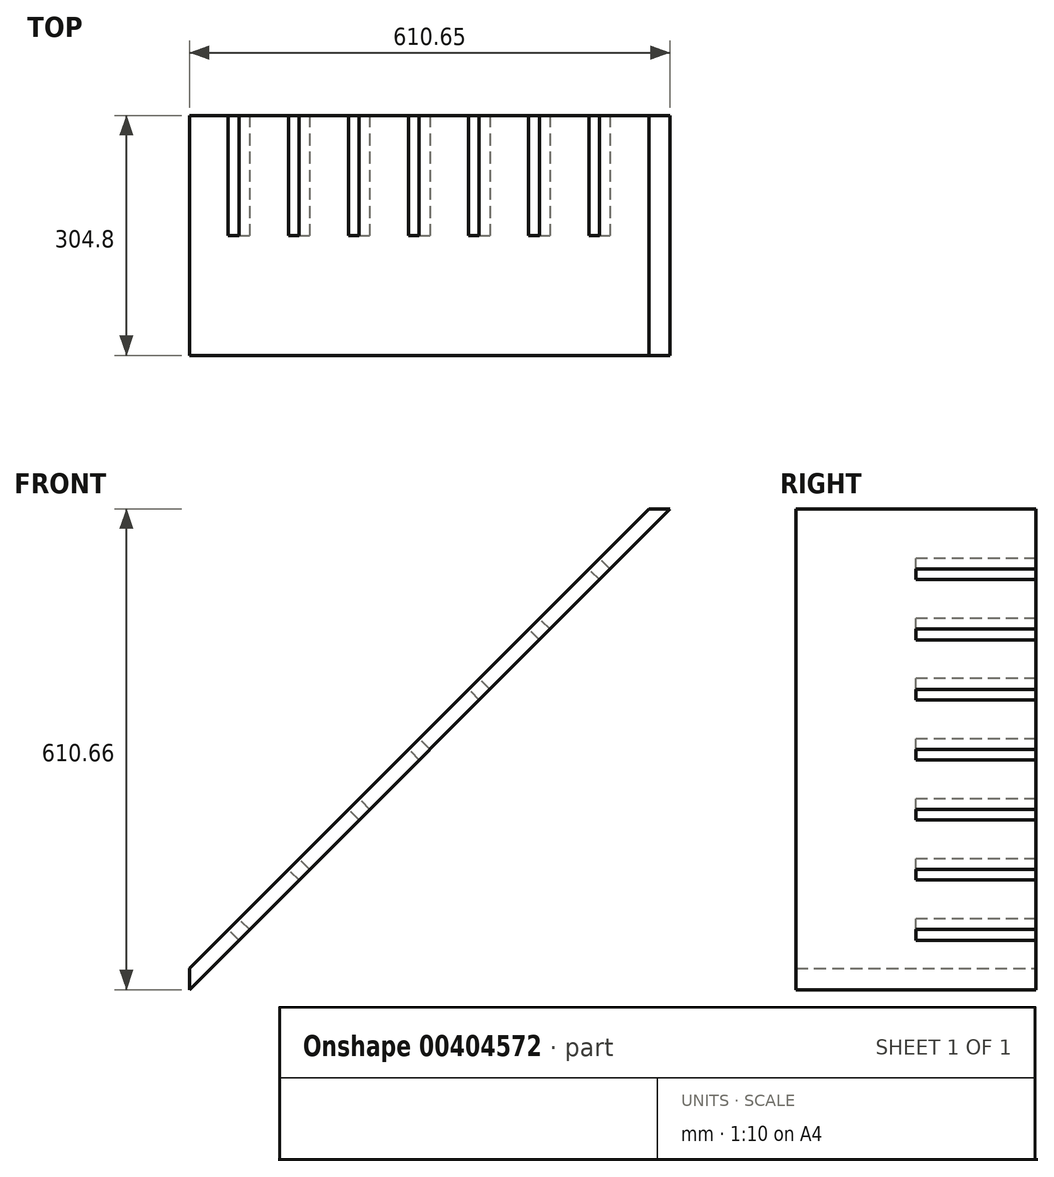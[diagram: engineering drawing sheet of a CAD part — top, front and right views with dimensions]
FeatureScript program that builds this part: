
annotation { "Feature Type Name" : "Feature", "Feature Type Description" : "" }
export const myFeature = defineFeature(function(context is Context, id is Id, definition is map)
    precondition{}
    {
        {
            var Q0;
            Q0=qCreatedBy(makeId("Front.planeOp"),FACE);
            var sketch = newSketch(context, id + "F0", { "sketchPlane" : qUnion([Q0])});
            skLineSegment(sketch, "E0.left", {"start": v(-421.52, 0) * mm, "end": v(-421.52, 26.94) * mm});
            skPoint(sketch, "E0.middle", {"position": v(22.97, 488.94) * mm});
            skLineSegment(sketch, "E1", {"start": v(-421.52, 0) * mm, "end": v(189.13, 610.66) * mm});
            skLineSegment(sketch, "E2", {"start": v(-421.52, 26.94) * mm, "end": v(162.2, 610.66) * mm});
            skLineSegment(sketch, "E3", {"start": v(189.13, 610.66) * mm, "end": v(162.2, 610.66) * mm});
            skSolve(sketch);
        }
        {
            var Q0;
            Q0=qSketchRegion(id+"F0",true);
            extrude(context, id + "F1", {"entities" : qUnion([Q0]), "endBound" : BoundingType.SYMMETRIC, "depth" : 304.8 * mm});
        }
        {
            var Q0;
            Q0=makeQuery(id+"F1.opExtrude","SWEPT_FACE",FACE,{"disambiguationData":[OSD([sQuery(id+"F0.wireOp",EDGE,"E2")])]});
            var sketch = newSketch(context, id + "F2", { "sketchPlane" : qUnion([Q0])});
            skLineSegment(sketch, "E4.bottom", {"start": v(-152.4, -209.16) * mm, "end": v(0, -209.16) * mm});
            skLineSegment(sketch, "E4.top", {"start": v(-152.4, -190.11) * mm, "end": v(0, -190.11) * mm});
            skLineSegment(sketch, "E4.left", {"start": v(-152.4, -209.16) * mm, "end": v(-152.4, -190.11) * mm});
            skLineSegment(sketch, "E4.right", {"start": v(0, -209.16) * mm, "end": v(0, -190.11) * mm});
            skLineSegment(sketch, "E5.bottom", {"start": v(-152.4, -101.21) * mm, "end": v(0, -101.21) * mm});
            skLineSegment(sketch, "E5.top", {"start": v(-152.4, -82.16) * mm, "end": v(0, -82.16) * mm});
            skLineSegment(sketch, "E5.left", {"start": v(-152.4, -101.21) * mm, "end": v(-152.4, -82.16) * mm});
            skLineSegment(sketch, "E5.right", {"start": v(0, -101.21) * mm, "end": v(0, -82.16) * mm});
            skLineSegment(sketch, "E6.bottom", {"start": v(-152.4, 6.74) * mm, "end": v(0, 6.74) * mm});
            skLineSegment(sketch, "E6.top", {"start": v(-152.4, 25.79) * mm, "end": v(0, 25.79) * mm});
            skLineSegment(sketch, "E6.left", {"start": v(-152.4, 6.74) * mm, "end": v(-152.4, 25.79) * mm});
            skLineSegment(sketch, "E6.right", {"start": v(0, 6.74) * mm, "end": v(0, 25.79) * mm});
            skLineSegment(sketch, "E7.bottom", {"start": v(-152.4, 114.69) * mm, "end": v(0, 114.69) * mm});
            skLineSegment(sketch, "E7.top", {"start": v(-152.4, 133.74) * mm, "end": v(0, 133.74) * mm});
            skLineSegment(sketch, "E7.left", {"start": v(-152.4, 114.69) * mm, "end": v(-152.4, 133.74) * mm});
            skLineSegment(sketch, "E7.right", {"start": v(0, 114.69) * mm, "end": v(0, 133.74) * mm});
            skLineSegment(sketch, "E8.bottom", {"start": v(-152.4, 222.64) * mm, "end": v(0, 222.64) * mm});
            skLineSegment(sketch, "E8.top", {"start": v(-152.4, 241.69) * mm, "end": v(0, 241.69) * mm});
            skLineSegment(sketch, "E8.left", {"start": v(-152.4, 222.64) * mm, "end": v(-152.4, 241.69) * mm});
            skLineSegment(sketch, "E8.right", {"start": v(0, 222.64) * mm, "end": v(0, 241.69) * mm});
            skLineSegment(sketch, "E9.bottom", {"start": v(-152.4, 330.59) * mm, "end": v(0, 330.59) * mm});
            skLineSegment(sketch, "E9.top", {"start": v(-152.4, 349.64) * mm, "end": v(0, 349.64) * mm});
            skLineSegment(sketch, "E9.left", {"start": v(-152.4, 330.59) * mm, "end": v(-152.4, 349.64) * mm});
            skLineSegment(sketch, "E9.right", {"start": v(0, 330.59) * mm, "end": v(0, 349.64) * mm});
            skLineSegment(sketch, "E10.bottom", {"start": v(-152.4, 438.54) * mm, "end": v(0, 438.54) * mm});
            skLineSegment(sketch, "E10.top", {"start": v(-152.4, 457.59) * mm, "end": v(0, 457.59) * mm});
            skLineSegment(sketch, "E10.left", {"start": v(-152.4, 438.54) * mm, "end": v(-152.4, 457.59) * mm});
            skLineSegment(sketch, "E10.right", {"start": v(0, 438.54) * mm, "end": v(0, 457.59) * mm});
            skSolve(sketch);
        }
        {
            var Q0;
            Q0=qSketchRegion(id+"F2",true);
            extrude(context, id + "F3", {"entities" : qUnion([Q0]), "operationType" : NewBodyOperationType.REMOVE, "oppositeDirection" : true, "depth" : 19.05 * mm});
        }
    });
